# Revit family: Door_Overhead-High-Speed_WayneDalton_Fabric-Rubber
name_source: partatom
category: Doors
revit_build: Autodesk Revit 2014 (Build: 20130308_1515(x64)
units: mm (PartAtom-declared; Revit-internal decimal feet)

## types (1)
- as Specified
    994 Model = No
    995 Model = No
    Air Infiltration = as Specified
    Angled Hood = No
    Assembly Code = B2030400
    Bottom Bar A = Yes
    Bottom Bar B = No
    Bottom Bar C = No
    Clearance_NonOperator Side = 1' - 8"
    Clearance_Operator Side = 1' - 8"
    Description = Wayne Dalton Product as Specified
    Expected Lifespan (Years) = 0
    Fire Rating = as Specified
    Function = Interior
    Height = 0' - 0"
    Hood Above Opening = 0' - 9 1/2"
    Hood Depth = 0' - 11 1/4"
    Hood Height = 0' - 11"
    Jamb Above Opening = 0' - 4 1/2"
    Jamb Depth = 0' - 4 7/16"
    Jamb Width = 0' - 6"
    Keynote = 08 33 23
    Maintenance Schedule (Months) = 0
    Manufacturer = Wayne Dalton
    Manufacturer Website = http://www.wayne-dalton.com
    Max Height = 0' - 0"
    Max Width = 0' - 0"
    Model = as Specified
    Operating Speed = as Specified
    Product Data = http://www.arcat.com
    Rough Height = 0' - 0"
    Rough Width = 0' - 0"
    Sales Information = http://www.wayne-dalton.com
    Solid Panel = Yes
    SpecWizard = http://www.arcat.com
    Specification = http://www.arcat.com
    Standards Conformance = as Specified
    Struts on Panel = Yes
    Thickness = 0' - 0"
    URL = http://www.wayne-dalton.com
    Vision Centerline = 5' - 5"
    Vision Panel = No
    Wall Closure = By host
    Warranty Duration (Years) = 0
    Width = 0' - 0"
    Wind Load = as Specified

## geometry (parser evidence)
native form markers: Blend x4, Sweep x8
no freeform markers — native parametric forms only
